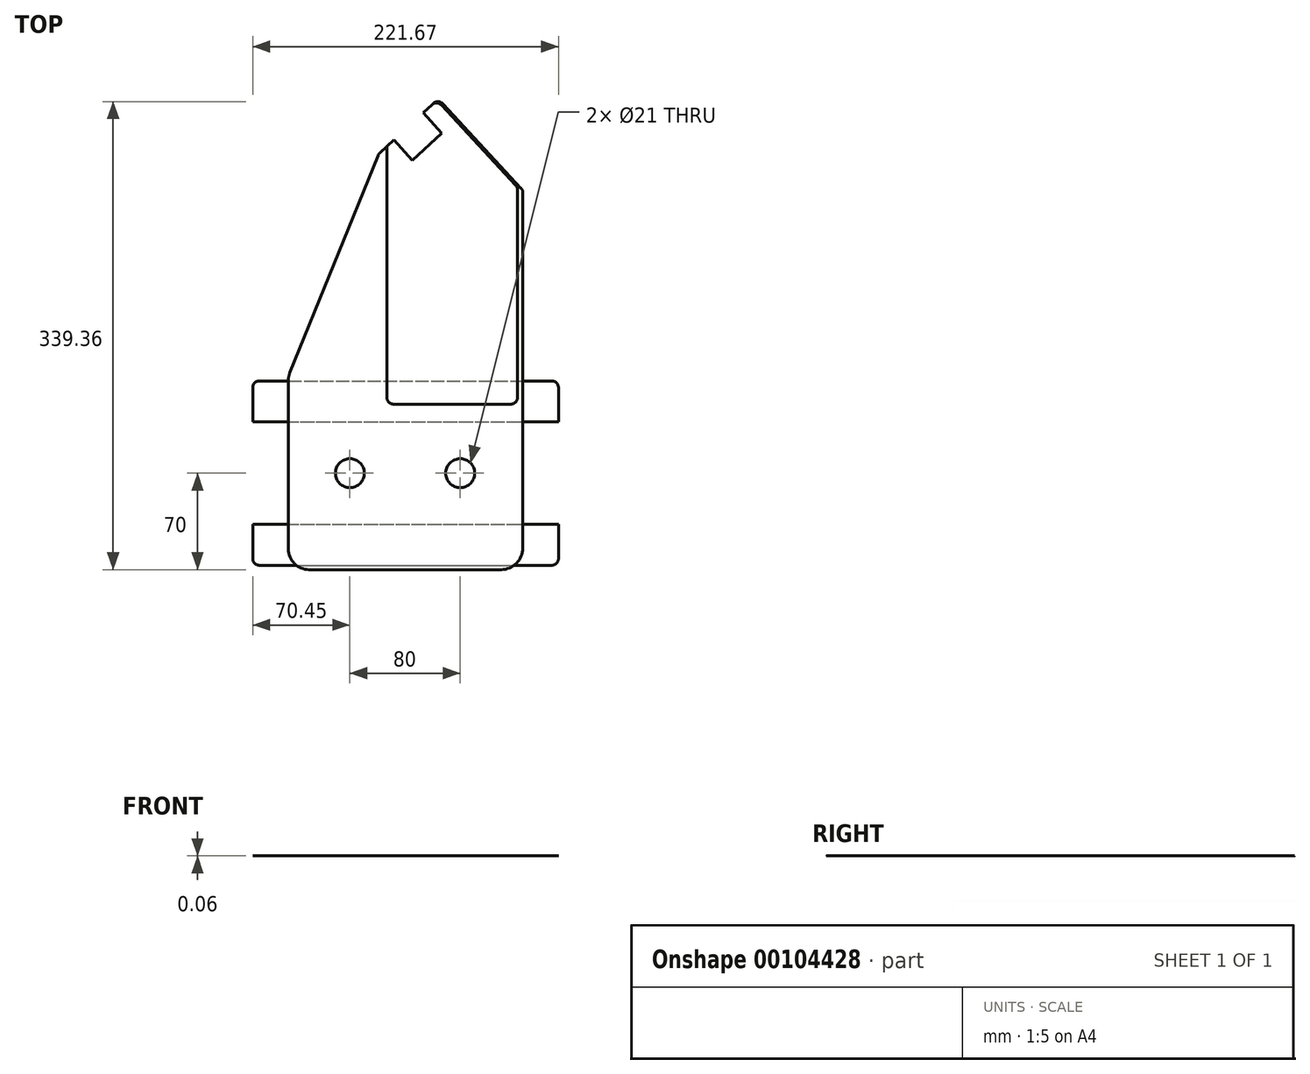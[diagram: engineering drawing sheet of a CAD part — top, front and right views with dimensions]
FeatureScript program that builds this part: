
annotation { "Feature Type Name" : "Feature", "Feature Type Description" : "" }
export const myFeature = defineFeature(function(context is Context, id is Id, definition is map)
    precondition{}
    {
        {
            var Q0;
            Q0=qCreatedBy(makeId("Top.planeOp"),FACE);
            var sketch = newSketch(context, id + "F0", { "sketchPlane" : qUnion([Q0])});
            skCircle(sketch, "E0", {"center": v(-40, 0) * mm, "radius": 10.5 * mm});
            skCircle(sketch, "E1", {"center": v(40, 0) * mm, "radius": 10.5 * mm});
            skLineSegment(sketch, "E2", {"start": v(-40, 0) * mm, "end": v(40, 0) * mm, "construction": true});
            skLineSegment(sketch, "E3", {"start": v(-69.58, -70) * mm, "end": v(69.58, -70) * mm});
            skPoint(sketch, "E4.visualSharp", {"position": v(85.42, -70) * mm});
            skArc(sketch, "E4.filletArc", {"start": v(69.58, -70) * mm, "mid": v(80.78, -65.36) * mm, "end": v(85.42, -54.17) * mm});
            skPoint(sketch, "E5.visualSharp", {"position": v(-84.58, -70) * mm});
            skArc(sketch, "E5.filletArc", {"start": v(-84.58, -55) * mm, "mid": v(-80.2, -65.6) * mm, "end": v(-69.58, -70) * mm});
            skPoint(sketch, "E6.visualSharp", {"position": v(-84.58, 70) * mm});
            skLineSegment(sketch, "E7", {"start": v(0, 120.47) * mm, "end": v(0, -70) * mm, "construction": true});
            skPoint(sketch, "E8", {"position": v(0, -70) * mm});
            skPoint(sketch, "E9", {"position": v(50, 200) * mm});
            skLineSegment(sketch, "E10", {"start": v(50, 200) * mm, "end": v(16.06, 236.71) * mm, "construction": true});
            skLineSegment(sketch, "E11", {"start": v(5.4, 226.87) * mm, "end": v(16.06, 236.71) * mm});
            skLineSegment(sketch, "E12", {"start": v(5.4, 226.87) * mm, "end": v(-8.17, 241.55) * mm});
            skLineSegment(sketch, "E13", {"start": v(-8.17, 241.55) * mm, "end": v(-18.36, 232.13) * mm});
            skLineSegment(sketch, "E14", {"start": v(-19.6, 230.34) * mm, "end": v(-83.49, 72.71) * mm});
            skLineSegment(sketch, "E15.MirrorCS", {"start": v(26.7, 246.56) * mm, "end": v(16.06, 236.71) * mm});
            skLineSegment(sketch, "E16.MirrorCS", {"start": v(26.7, 246.56) * mm, "end": v(13.13, 261.24) * mm});
            skLineSegment(sketch, "E17.MirrorCS", {"start": v(13.13, 261.24) * mm, "end": v(20.47, 268.03) * mm});
            skLineSegment(sketch, "E18", {"start": v(85.42, -54.17) * mm, "end": v(85.42, 203.2) * mm});
            skLineSegment(sketch, "E19", {"start": v(-84.58, -55) * mm, "end": v(-84.58, 67.08) * mm});
            skLineSegment(sketch, "E20", {"start": v(27.53, 267.75) * mm, "end": v(84.09, 206.59) * mm});
            skPoint(sketch, "E21.visualSharp", {"position": v(85.42, 205.15) * mm});
            skArc(sketch, "E21.filletArc", {"start": v(85.42, 203.2) * mm, "mid": v(85.07, 205.01) * mm, "end": v(84.09, 206.59) * mm});
            skPoint(sketch, "E22.visualSharp", {"position": v(24.14, 271.42) * mm});
            skArc(sketch, "E22.filletArc", {"start": v(27.53, 267.75) * mm, "mid": v(24.06, 269.36) * mm, "end": v(20.47, 268.03) * mm});
            skPoint(sketch, "E23.visualSharp", {"position": v(-19.18, 231.37) * mm});
            skArc(sketch, "E23.filletArc", {"start": v(-18.36, 232.13) * mm, "mid": v(-19.08, 231.3) * mm, "end": v(-19.6, 230.34) * mm});
            skArc(sketch, "E24.filletArc", {"start": v(-83.49, 72.71) * mm, "mid": v(-84.3, 69.95) * mm, "end": v(-84.58, 67.08) * mm});
            skSolve(sketch);
        }
        {
            var Q0;
            Q0=makeQuery(id+"F0.imprint","IMPRINT",FACE,{"disambiguationData":[TD([[makeQuery(id+"F0.imprint","IMPRINT",EDGE,{"derivedFrom":sQuery(id+"F0.wireOp",EDGE,"E0")}),-1.0]])]});
            extrude(context, id + "F1", {"entities" : qUnion([Q0]), "depth" : 9 / 406.4 * mm});
        }
        {
            var Q0;
            Q0=makeQuery(id+"F1.opExtrude","CAP_FACE",FACE,{"disambiguationData":[OSD([sQuery(id+"F0.wireOp",EDGE,"E0"),sQuery(id+"F0.wireOp",EDGE,"E1"),sQuery(id+"F0.wireOp",EDGE,"ORsLJO4S-Lcrg-lpuZ-IpTO-JsHhmnabdJaW"),sQuery(id+"F0.wireOp",EDGE,"E3"),sQuery(id+"F0.wireOp",EDGE,"GkN3tyXG-18Eo-Ar0N-vTS5-nBuOveoUkN9s"),sQuery(id+"F0.wireOp",EDGE,"xwqs8ldE-Amip-0tNx-dzJk-uVIK760CaaNG"),sQuery(id+"F0.wireOp",EDGE,"AQNgvmri-sfpQ-wzMW-YrrT-fI6N64ai6BJn"),sQuery(id+"F0.wireOp",EDGE,"EPBhpeX1-9vd9-T2Hr-ksZR-klpsxm78xYMp"),sQuery(id+"F0.wireOp",EDGE,"4de21265-d169-4b6b-aa7f-9020d00b30fa.filletArc"),sQuery(id+"F0.wireOp",EDGE,"c0dfad71-8511-4710-93e8-2a922c9cec26.filletArc"),sQuery(id+"F0.wireOp",EDGE,"E4.filletArc"),sQuery(id+"F0.wireOp",EDGE,"E5.filletArc"),sQuery(id+"F0.wireOp",EDGE,"E6.filletArc")])],"isStart":true});
            var sketch = newSketch(context, id + "F2", { "sketchPlane" : qUnion([Q0])});
            skLineSegment(sketch, "E25.bottom", {"start": v(-105.45, -66.89) * mm, "end": v(106.22, -66.89) * mm});
            skLineSegment(sketch, "E25.top", {"start": v(-110.45, -37.2) * mm, "end": v(111.22, -37.2) * mm});
            skLineSegment(sketch, "E25.left", {"start": v(-110.45, -61.89) * mm, "end": v(-110.45, -37.2) * mm});
            skLineSegment(sketch, "E25.right", {"start": v(111.22, -61.89) * mm, "end": v(111.22, -37.2) * mm});
            skPoint(sketch, "E26.visualSharp", {"position": v(-110.45, -66.89) * mm});
            skArc(sketch, "E26.filletArc", {"start": v(-110.45, -61.89) * mm, "mid": v(-108.98, -65.42) * mm, "end": v(-105.45, -66.89) * mm});
            skPoint(sketch, "E27.visualSharp", {"position": v(111.22, -66.89) * mm});
            skArc(sketch, "E27.filletArc", {"start": v(106.22, -66.89) * mm, "mid": v(109.76, -65.42) * mm, "end": v(111.22, -61.89) * mm});
            skArc(sketch, "E28.MirrorCS", {"start": v(106.22, 66.89) * mm, "mid": v(109.76, 65.42) * mm, "end": v(111.22, 61.89) * mm});
            skArc(sketch, "E29.MirrorCS", {"start": v(-110.45, 61.89) * mm, "mid": v(-108.98, 65.42) * mm, "end": v(-105.45, 66.89) * mm});
            skPoint(sketch, "E30.MirrorP", {"position": v(-110.45, 66.89) * mm});
            skPoint(sketch, "E31.MirrorP", {"position": v(111.22, 66.89) * mm});
            skLineSegment(sketch, "E32.MirrorCS", {"start": v(-105.45, 66.89) * mm, "end": v(106.22, 66.89) * mm});
            skLineSegment(sketch, "E33.MirrorCS", {"start": v(-110.45, 37.2) * mm, "end": v(111.22, 37.2) * mm});
            skLineSegment(sketch, "E34.MirrorCS", {"start": v(-110.45, 61.89) * mm, "end": v(-110.45, 37.2) * mm});
            skLineSegment(sketch, "E35.MirrorCS", {"start": v(111.22, 61.89) * mm, "end": v(111.22, 37.2) * mm});
            skSolve(sketch);
        }
        {
            var Q0;
            {var subQ0=sQuery(id+"F2.wireOp",EDGE,"E25.left");Q0=makeQuery(id+"F2.imprint","IMPRINT",FACE,{"disambiguationData":[TD([[makeQuery(id+"F2.imprint","IMPRINT",EDGE,{"derivedFrom":subQ0}),-1.0]])]});}
            var Q1;
            {var subQ5=sQuery(id+"F2.wireOp",EDGE,"E25.bottom");var subQ9=makeQuery(id+"F1.opExtrude","CAP_EDGE",EDGE,{"disambiguationData":[OSD([sQuery(id+"F0.wireOp",EDGE,"E5.filletArc")])],"isStart":false});var subQ11=makeQuery(id+"F2.imprint","INTERSECT",VERTEX,{"derivedFrom":[subQ9,subQ5]});Q1=makeQuery(id+"F2.imprint","IMPRINT",FACE,{"disambiguationData":[TD([[makeQuery(id+"F2.imprint","IMPRINT",EDGE,{"disambiguationData":[TD([[subQ11,-1.0]])],"derivedFrom":subQ5}),1.0]])]});}
            var Q2;
            {var subQ0=sQuery(id+"F2.wireOp",EDGE,"E25.right");Q2=makeQuery(id+"F2.imprint","IMPRINT",FACE,{"disambiguationData":[TD([[makeQuery(id+"F2.imprint","IMPRINT",EDGE,{"derivedFrom":subQ0}),1.0]])]});}
            var Q3;
            {var subQ5=sQuery(id+"F2.wireOp",EDGE,"E28.MirrorCS");Q3=makeQuery(id+"F2.imprint","IMPRINT",FACE,{"disambiguationData":[TD([[makeQuery(id+"F2.imprint","IMPRINT",EDGE,{"derivedFrom":subQ5}),-1.0]])]});}
            var Q4;
            {var subQ0=sQuery(id+"F2.wireOp",EDGE,"E32.MirrorCS");var subQ5=makeQuery(id+"F1.opExtrude","CAP_EDGE",EDGE,{"disambiguationData":[OSD([sQuery(id+"F0.wireOp",EDGE,"E6.filletArc")])],"isStart":false});var subQ9=makeQuery(id+"F2.imprint","INTERSECT",VERTEX,{"derivedFrom":[subQ5,subQ0]});Q4=makeQuery(id+"F2.imprint","IMPRINT",FACE,{"disambiguationData":[TD([[makeQuery(id+"F2.imprint","IMPRINT",EDGE,{"disambiguationData":[TD([[subQ9,-1.0]])],"derivedFrom":subQ0}),-1.0]])]});}
            var Q5;
            {var subQ5=sQuery(id+"F2.wireOp",EDGE,"E29.MirrorCS");Q5=makeQuery(id+"F2.imprint","IMPRINT",FACE,{"disambiguationData":[TD([[makeQuery(id+"F2.imprint","IMPRINT",EDGE,{"derivedFrom":subQ5}),-1.0]])]});}
            extrude(context, id + "F3", {"entities" : qUnion([Q0, Q1, Q2, Q3, Q4, Q5]), "depth" : 9 / 406.4 * mm});
        }
        {
            var Q0;
            Q0=makeQuery(id+"F1.opExtrude","CAP_FACE",FACE,{"disambiguationData":[OSD([sQuery(id+"F0.wireOp",EDGE,"E0"),sQuery(id+"F0.wireOp",EDGE,"E1"),sQuery(id+"F0.wireOp",EDGE,"ORsLJO4S-Lcrg-lpuZ-IpTO-JsHhmnabdJaW"),sQuery(id+"F0.wireOp",EDGE,"E3"),sQuery(id+"F0.wireOp",EDGE,"GkN3tyXG-18Eo-Ar0N-vTS5-nBuOveoUkN9s"),sQuery(id+"F0.wireOp",EDGE,"xwqs8ldE-Amip-0tNx-dzJk-uVIK760CaaNG"),sQuery(id+"F0.wireOp",EDGE,"AQNgvmri-sfpQ-wzMW-YrrT-fI6N64ai6BJn"),sQuery(id+"F0.wireOp",EDGE,"EPBhpeX1-9vd9-T2Hr-ksZR-klpsxm78xYMp"),sQuery(id+"F0.wireOp",EDGE,"4de21265-d169-4b6b-aa7f-9020d00b30fa.filletArc"),sQuery(id+"F0.wireOp",EDGE,"c0dfad71-8511-4710-93e8-2a922c9cec26.filletArc"),sQuery(id+"F0.wireOp",EDGE,"E4.filletArc"),sQuery(id+"F0.wireOp",EDGE,"E5.filletArc"),sQuery(id+"F0.wireOp",EDGE,"E6.filletArc")])],"isStart":false});
            var sketch = newSketch(context, id + "F4", { "sketchPlane" : qUnion([Q0])});
            skLineSegment(sketch, "E36", {"start": v(76.55, 49.96) * mm, "end": v(-8.26, 49.96) * mm});
            skArc(sketch, "E37.filletArc", {"start": v(76.55, 49.96) * mm, "mid": v(80.09, 51.43) * mm, "end": v(81.55, 54.96) * mm});
            skArc(sketch, "E38.filletArc", {"start": v(-13.26, 54.96) * mm, "mid": v(-11.8, 51.43) * mm, "end": v(-8.26, 49.96) * mm});
            skLineSegment(sketch, "E39", {"start": v(13.13, 261.24) * mm, "end": v(26.7, 246.56) * mm});
            skLineSegment(sketch, "E40", {"start": v(26.7, 246.56) * mm, "end": v(5.4, 226.87) * mm});
            skLineSegment(sketch, "E41", {"start": v(5.4, 226.87) * mm, "end": v(-8.17, 241.55) * mm});
            skLineSegment(sketch, "E42", {"start": v(-8.17, 241.55) * mm, "end": v(-13.26, 236.84) * mm});
            skLineSegment(sketch, "E43", {"start": v(-13.26, 236.84) * mm, "end": v(-13.26, 54.96) * mm});
            skLineSegment(sketch, "E44", {"start": v(81.55, 54.96) * mm, "end": v(81.55, 205.28) * mm});
            skLineSegment(sketch, "E45", {"start": v(80.23, 208.68) * mm, "end": v(26.5, 266.8) * mm});
            skLineSegment(sketch, "E46", {"start": v(19.43, 267.07) * mm, "end": v(13.13, 261.24) * mm});
            skPoint(sketch, "E47.visualSharp", {"position": v(23.1, 270.46) * mm});
            skArc(sketch, "E47.filletArc", {"start": v(26.5, 266.8) * mm, "mid": v(23.02, 268.4) * mm, "end": v(19.43, 267.07) * mm});
            skPoint(sketch, "E48.visualSharp", {"position": v(81.55, 207.24) * mm});
            skArc(sketch, "E48.filletArc", {"start": v(81.55, 205.28) * mm, "mid": v(81.2, 207.1) * mm, "end": v(80.23, 208.68) * mm});
            skSolve(sketch);
        }
        {
            var Q0;
            Q0 = qSketchRegion(id + "F4", true);
            extrude(context, id + "F5", {"entities" : qUnion([Q0]), "operationType" : NewBodyOperationType.ADD, "depth" : 9 / 406.4 * mm, "offsetDistance" : 25 * mm});
        }
    });
